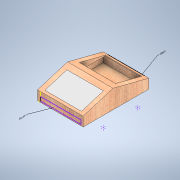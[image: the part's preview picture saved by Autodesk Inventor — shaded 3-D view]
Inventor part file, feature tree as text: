
AUTODESK INVENTOR PART (.ipt)
format: ipt  version: 2020 (Build 240168000, 168)  size: 169,984 bytes
history: native  units: in
note: dims shown in document units (in); Inventor stores cm internally (conversion verified against a paired STEP export)
features: sketch x7, extrude x4, other x3, shell x1
ambient origin geometry x8: Origin, YZ Plane, XZ Plane, XY Plane, X Axis, Y Axis, Z Axis, Center Point
bodies: Solid1 (feature_tree), Solid4 (feature_tree)
feature tree (15):
  other  "Annotations"
  extrude  "Extrusion1"  Depth=14.1732in
  shell  "Shell1"  Thickness=2.0472in
  sketch  "3D Sketch5"
  extrude  "Extrusion4"  Depth=0.5906in
  extrude  "Extrusion5"  Depth=0.9843in
  sketch  "Sketch10"  dims[d31=0.9843in d32=1.1811in d33=0.0in]
  sketch  "Sketch11"  dims[d34=0.0787in d35=0.0in]
  extrude  "Extrusion6"  Depth=1.1811in TaperAngle=0.0deg
  sketch  "Sketch1"  dims[d0=9.8425in d1=14.1732in d2=2.0472in d3=0.0in]
  sketch  "Sketch8"  dims[d4=0.5906in d27=0.1168in]
  sketch  "Sketch9"  dims[d28=0.3937in d29=0.0in d30=0.9843in]
  sketch  "Sketch12"  dims[d5=0.1354in d6=0.0742in d7=0.0893in d8=0.1577in d36=0.1969in d37=0.0344in]
  other  "Leader Text 1"
  other  "Leader Text 2"
